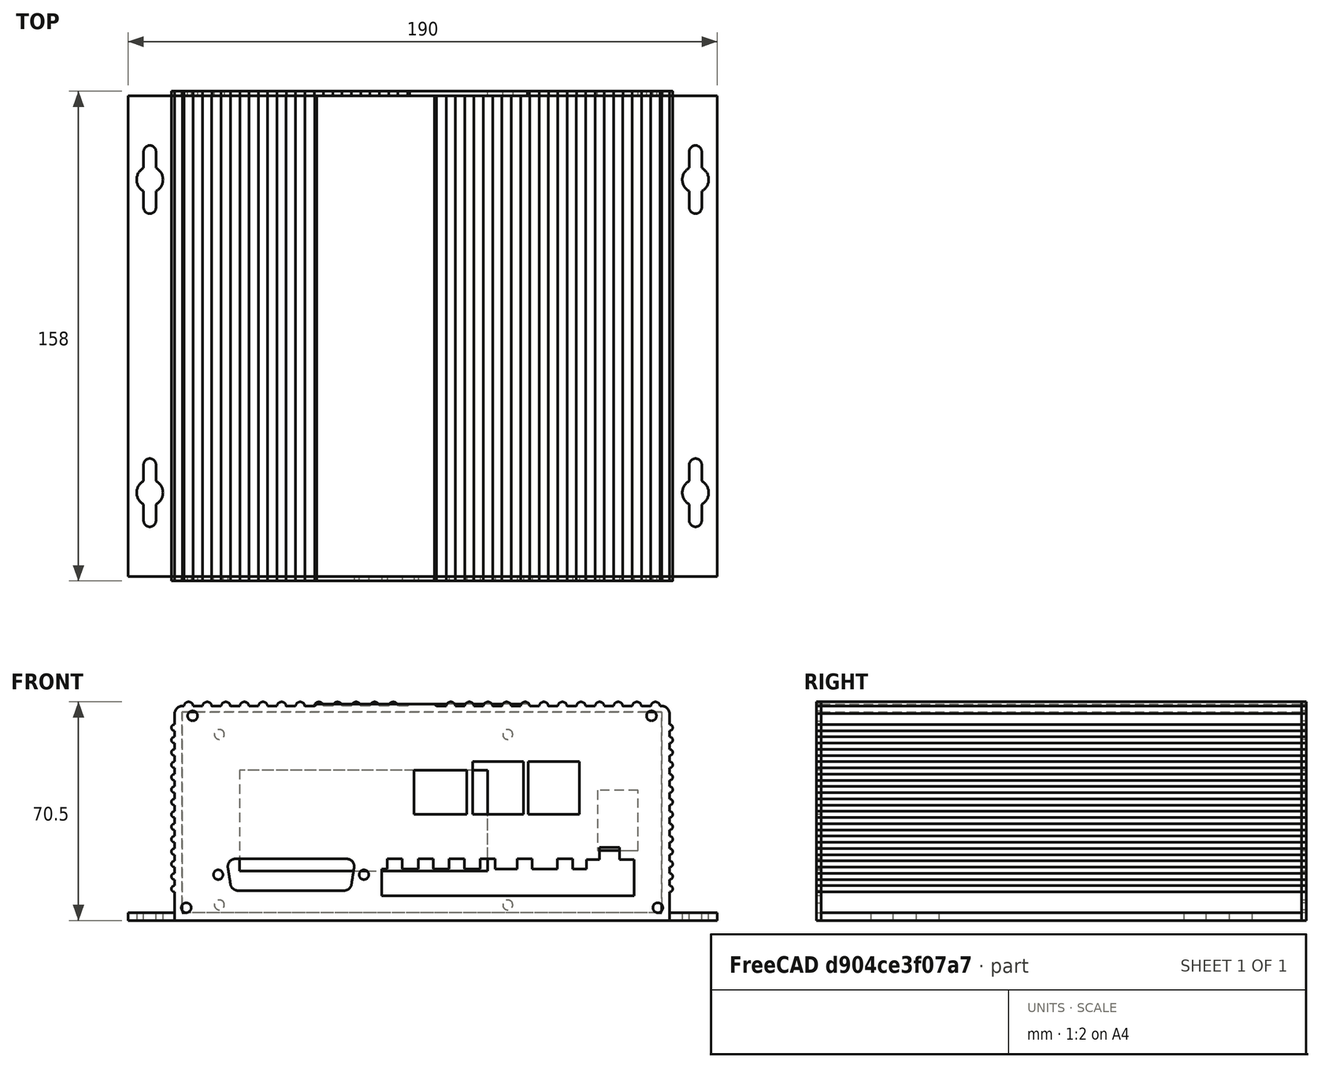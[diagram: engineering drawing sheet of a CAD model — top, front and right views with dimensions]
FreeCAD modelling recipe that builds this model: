
FCSTD DOCUMENT  (FreeCAD 0.16R)
Label: enclosure
License: All rights reserved
LicenseURL: http://en.wikipedia.org/wiki/All_rights_reserved
objects: Part::Feature×30, Part::Extrusion×30, Part::MultiFuse×4, Part::Cut×4
note: 68 computed .brp shape members not serialized (recipe doc carries the construction recipe); baked Part::Feature solids carry a one-line shape summary decoded from their .brp

FEATURE [Part::Feature] Face
  shape: bbox 190 x 155 x 2e-07 mm, 1 faces, 0 solids (baked)
FEATURE [Part::Extrusion] Extrude
  Base = -> Face
  Dir = (0,0,2.5)
  Solid = true
FEATURE [Part::Feature] Face001 .. Face004  x4 (patterned run collapsed; names and placements below)
  shape: bbox 8.5 x 22 x 2e-07 mm, 1 faces, 0 solids (baked)
FEATURE [Part::Extrusion] Extrude001
  Base = -> Face001
  Dir = (0,0,3)
  Solid = true
FEATURE [Part::Extrusion] Extrude002
  Base = -> Face002
  Dir = (0,0,3)
  Solid = true
FEATURE [Part::Extrusion] Extrude003
  Base = -> Face003
  Dir = (0,0,3)
  Solid = true
FEATURE [Part::Extrusion] Extrude004
  Base = -> Face004
  Dir = (0,0,3)
  Solid = true
FEATURE [Part::MultiFuse] Fusion
  Shapes = -> [Extrude001,Extrude002,Extrude004,Extrude003]
FEATURE [Part::Cut] Cut
  Base = -> Extrude
  Tool = -> Fusion
FEATURE [Part::Feature] Face005
  shape: bbox 161.7 x 2e-07 x 70.5 mm, 1 faces, 0 solids (baked)
FEATURE [Part::Extrusion] Extrude005
  Base = -> Face005
  Dir = (0,155,0)
  Solid = true
FEATURE [Part::MultiFuse] Fusion001
  Shapes = -> [Extrude005,Cut]
FEATURE [Part::Feature] Face015
  Placement = pos=(15.15,0,0) rot=(1,0,0;1.5708rad)
  shape: bbox 154.7 x 2e-07 x 64.8 mm, 1 faces, 0 solids (baked)
FEATURE [Part::Extrusion] Extrude015
  Base = -> Face015
  Dir = (0,155.5,0)
  Solid = false
FEATURE [Part::Cut] Cut003  label="Body"
  Base = -> Fusion001
  Tool = -> Extrude015
FEATURE [Part::Feature] Face016
  shape: bbox 161.7 x 70.5 x 2e-07 mm, 1 faces, 0 solids (baked)
FEATURE [Part::Feature] Face019
  shape: bbox 41.08 x 10.22 x 2e-07 mm, 1 faces, 0 solids (baked)
FEATURE [Part::Feature] Face020
  shape: bbox 16.45 x 17 x 2e-07 mm, 1 faces, 0 solids (baked)
FEATURE [Part::Feature] Face021
  shape: bbox 16.45 x 17 x 2e-07 mm, 1 faces, 0 solids (baked)
FEATURE [Part::Feature] Face022
  shape: bbox 17.01 x 14.25 x 2e-07 mm, 1 faces, 0 solids (baked)
FEATURE [Part::Feature] Face023
  shape: bbox 81.33 x 15.6 x 2e-07 mm, 1 faces, 0 solids (baked)
FEATURE [Part::Feature] Face027
  shape: bbox 3.2 x 3.2 x 2e-07 mm, 1 faces, 0 solids (baked)
FEATURE [Part::Feature] Face028
  shape: bbox 3.2 x 3.2 x 2e-07 mm, 1 faces, 0 solids (baked)
FEATURE [Part::Feature] Face026
  shape: bbox 3.2 x 3.2 x 2e-07 mm, 1 faces, 0 solids (baked)
FEATURE [Part::Feature] Face032
  shape: bbox 3.2 x 3.2 x 2e-07 mm, 1 faces, 0 solids (baked)
FEATURE [Part::Feature] Face031
  shape: bbox 3.1 x 3.1 x 2e-07 mm, 1 faces, 0 solids (baked)
FEATURE [Part::Feature] Face030
  shape: bbox 3.1 x 3.1 x 2e-07 mm, 1 faces, 0 solids (baked)
FEATURE [Part::Extrusion] Extrude016
  Base = -> Face016
  Dir = (0,0,1.5)
  Solid = false
FEATURE [Part::Extrusion] Extrude018
  Base = -> Face019
  Dir = (0,0,6.35)
  Solid = false
FEATURE [Part::Extrusion] Extrude019
  Base = -> Face020
  Dir = (0,0,6.35)
  Solid = false
FEATURE [Part::Extrusion] Extrude020
  Base = -> Face021
  Dir = (0,0,6.35)
  Solid = false
FEATURE [Part::Extrusion] Extrude021
  Base = -> Face022
  Dir = (0,0,6.35)
  Solid = false
FEATURE [Part::Extrusion] Extrude022
  Base = -> Face023
  Dir = (0,0,6.35)
  Solid = false
FEATURE [Part::Extrusion] Extrude023
  Base = -> Face027
  Dir = (0,0,6.35)
  Solid = false
FEATURE [Part::Extrusion] Extrude025
  Base = -> Face028
  Dir = (0,0,6.35)
  Solid = false
FEATURE [Part::Extrusion] Extrude026
  Base = -> Face026
  Dir = (0,0,6.35)
  Solid = true
FEATURE [Part::Extrusion] Extrude028
  Base = -> Face032
  Dir = (0,0,6.35)
  Solid = false
FEATURE [Part::Extrusion] Extrude029
  Base = -> Face031
  Dir = (0,0,6.35)
  Solid = false
FEATURE [Part::Extrusion] Extrude030
  Base = -> Face030
  Dir = (0,0,6.35)
  Solid = false
FEATURE [Part::MultiFuse] Fusion004
  Shapes = -> [Extrude030,Extrude018,Extrude019,Extrude020,Extrude021,Extrude022,Extrude023,Extrude025,Extrude026,Extrude028,Extrude029]
FEATURE [Part::Cut] Cut004  label="Back"
  Base = -> Extrude016
  Placement = pos=(15.15,0,0) rot=(1,0,0;1.5708rad)
  Tool = -> Fusion004
FEATURE [Part::Feature] Wire
  Placement = pos=(3.6,4.1,0) rot=(0,0,1;0rad)
  shape: bbox 3.2 x 3.2 x 2e-07 mm, 0 faces, 0 solids (baked)
FEATURE [Part::Feature] Wire001
  Placement = pos=(5.64592,65.9653,0) rot=(0,0,1;0rad)
  shape: bbox 3.2 x 3.2 x 2e-07 mm, 0 faces, 0 solids (baked)
FEATURE [Part::Feature] Wire002
  Placement = pos=(153.65,66,0) rot=(0,0,1;0rad)
  shape: bbox 3.2 x 3.2 x 2e-07 mm, 0 faces, 0 solids (baked)
FEATURE [Part::Feature] Wire003
  Placement = pos=(155.7,4.1,0) rot=(0,0,1;0rad)
  shape: bbox 3.2 x 3.2 x 2e-07 mm, 0 faces, 0 solids (baked)
FEATURE [Part::Feature] Wire004
  Placement = pos=(145,60,0) rot=(0,0,1;0rad)
  shape: bbox 3.2 x 3.2 x 2e-07 mm, 0 faces, 0 solids (baked)
FEATURE [Part::Feature] Wire005
  Placement = pos=(145,5,0) rot=(0,0,1;0rad)
  shape: bbox 3.2 x 3.2 x 2e-07 mm, 0 faces, 0 solids (baked)
FEATURE [Part::Feature] Wire006
  Placement = pos=(52,5,0) rot=(0,0,1;0rad)
  shape: bbox 3.2 x 3.2 x 2e-07 mm, 0 faces, 0 solids (baked)
FEATURE [Part::Feature] Wire007
  Placement = pos=(52,60,0) rot=(0,0,1;0rad)
  shape: bbox 3.2 x 3.2 x 2e-07 mm, 0 faces, 0 solids (baked)
FEATURE [Part::Feature] Wire008
  shape: bbox 13 x 19.4 x 2e-07 mm, 0 faces, 0 solids (baked)
FEATURE [Part::Feature] Wire009
  shape: bbox 80 x 32.5 x 2e-07 mm, 0 faces, 0 solids (baked)
FEATURE [Part::Feature] Wire010
  shape: bbox 161.7 x 70.5 x 2e-07 mm, 0 faces, 0 solids (baked)
FEATURE [Part::Extrusion] Extrude031
  Base = -> Wire010
  Dir = (0,0,1.5)
  Placement = pos=(0,0,0) rot=(0,0.707107,0.707107;3.14159rad)
  Solid = true
FEATURE [Part::Extrusion] Extrude032
  Base = -> Wire
  Dir = (0,0,2)
  Solid = true
FEATURE [Part::Extrusion] Extrude033
  Base = -> Wire001
  Dir = (0,0,2)
  Solid = true
FEATURE [Part::Extrusion] Extrude034
  Base = -> Wire002
  Dir = (0,0,2)
  Solid = true
FEATURE [Part::Extrusion] Extrude035
  Base = -> Wire003
  Dir = (0,0,2)
  Solid = true
FEATURE [Part::Extrusion] Extrude036
  Base = -> Wire004
  Dir = (0,0,2)
  Solid = true
FEATURE [Part::Extrusion] Extrude037
  Base = -> Wire005
  Dir = (0,0,2)
  Solid = true
FEATURE [Part::Extrusion] Extrude038
  Base = -> Wire006
  Dir = (0,0,2)
  Solid = true
FEATURE [Part::Extrusion] Extrude039
  Base = -> Wire007
  Dir = (0,0,2)
  Solid = true
FEATURE [Part::Extrusion] Extrude040
  Base = -> Wire008
  Dir = (0,0,2)
  Solid = true
FEATURE [Part::Extrusion] Extrude041
  Base = -> Wire009
  Dir = (0,0,2)
  Solid = true
FEATURE [Part::MultiFuse] Fusion005
  Placement = pos=(0,0,0) rot=(0,0.707107,0.707107;3.14159rad)
  Shapes = -> [Extrude032,Extrude041,Extrude035,Extrude036,Extrude040,Extrude033,Extrude034,Extrude039,Extrude037,Extrude038]
FEATURE [Part::Cut] Cut005  label="Front"
  Base = -> Extrude031
  Placement = pos=(174.45,155,0) rot=(0,0,1;0rad)
  Tool = -> Fusion005
